# Revit family: 22-CHLI
name_source: partatom
category: Aparatos sanitarios
units: mm (PartAtom-declared; Revit-internal decimal feet)

## family parameters
Activar corte en vistas = No
Compartido = No
Corte con vacíos al cargar = No
Cota de conector redondo = Usar diámetro
Mantener orientación de anotación = No
Número OmniClass = 23.45.00.00
Punto de cálculo de habitación = No
Se basa en plano de trabajo = No
Siempre vertical = Sí
Tipo de pieza = Normal
Título OmniClass = Sanitary, Laundry, and Cleaning Equipment

## types (1)
- 22-CHLI
    Body = Iron, Cast
    Comentarios de tipo = Coladera para Piso
    Conexión AF = Sí
    Conexión de ventilación = Sí
    Descripción = Coladera corta de una boca para inserto cuadrado, cromo. Incluye plato de drenado para evitar filtraciones. Contra con altura ajustable. Céspol que genera sello hidráulico para evitar malos olores. Fácil mantenimiento. Recomendable para baños, regaderas, vestíbulos y otras áreas interiores de pisos a nivel de planta y entrepisos.
    Drain = Brass Chromed
    Elevación por defecto = 0"
    Fabricante = HELVEX S.A. DE C.V.
    Garantía = El producto HELVEX está garantizado como libre de defectos en materiales y procesos de fabricación. El producto HELVEX está garantizado, en lo que se refiere a los acabados; por un periodo de 10 años en los acabados cromo y duravex, y por 2 años en cabados diferentes al cromo, a partir de la fecha de compra indicada en la factura.
    Grid = Stainless Steel
    Installation Thread = Diameter 2" NPSM (5.0 cm)
    Material = Porta inserto y contra de latón. Cuerpo de hierro fundido con recubrimiento de 
pintura anticorrosiva.
    Modelo = 22-CHLI
    Total Diameter = 7"

## geometry (parser evidence)
native form markers: Sweep x3
no freeform markers — native parametric forms only
